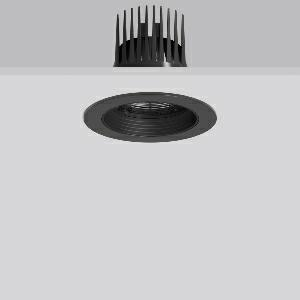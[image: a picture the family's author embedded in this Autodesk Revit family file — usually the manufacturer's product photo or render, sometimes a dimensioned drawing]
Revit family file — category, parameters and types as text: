
# Revit family: heledon_maxi_e_901767_003_1_76_1d41
name_source: partatom
category: Lighting Fixtures
units: mm (PartAtom-declared; Revit-internal decimal feet)

## family parameters
Cut with Voids When Loaded = No
Host = Face
Light Source = No
Part Type = Normal
Room Calculation Point = No
Round Connector Dimension = Use Diameter
Shared = No

## types (1)
- HELEDON maxi E (1 x LED Modul 940, 3900 lm, 4000)
    Apparent Load = 35 VA
    Approval mark = CE
    CIE Flux Codes = 97 100 100 100 100
    Color Rendering = 92
    Color Temperature = 4000
    Default Elevation = 1800 mm
    Description = Series: HELEDON maxi
Round recessed downlight. Housing: die-cast aluminium, powder-coated. Black plastic ring and recessed LED to prevent glare from the side. Optical assembly with lens made of plastic (polycarbonate) for the best homogeneous light distribution - can be changed without tools. Best colour rendering index Ra>90. Suitable for Recessed ceiling mounting. Installation without tools thanks to spring fastening system. Including separate LED converter with connecting cable 600 mm.High quality converter without flickering and stroboscopic effect. Through-wiring box (5 pole) available as accessory. The following accessories can be mounted without use of tools: interchangeable lenses, decorative glasses, honeycomb louvre, clear and frosted diffusers, white interchangeable plastic ring. 
Colour: deep black, matt (RAL 9005)
Diameter: 162 mm
Height: 3 mm
Cut-out diameter: 152 mm
Recess height: 200 mm
Luminaire: recess height: 135 mm
Lamp: LED
Socket: without socket
Colour temperature: 4000K
Colour rendering index (CRI): 92
System power: 35 W
Rated luminous flux: 3900 lm
Luminous efficiency: 111 lm/W
Control gear: Converter, dimmable, DALI
Protection class: II
Type of protection: IP 20
    Height = 0 mm  [stored 0 ft]
    Lamp = 1 x LED Modul 940
    Lamp Light Flux = 3900 lm
    Lamp count = 1
    Length = 162 mm
    Lifetime = 50000 h
    Luminous efficacy = 111 lm/W
    Manufacturer = RZB
    ModVariant = No
    Model = 901767.003.1.76
    Mounting Place = Ceiling
    Mounting Type = Recessed
    Number of Poles = 1
    OnlyDefault = Yes
    Power Factor = 1
    Product Name = HELEDON maxi E
    Product group = Recessed downlights
    ProductGroupID = 402
    Protection Class = Protection class II
    Protection Degree = IP 20
    RLX_Detail_Level = 1
    RLX_Emergency_Light_Flux = 0 lm
    RLX_Emergency_Type = 0
    RLX_Emergency_Type_DB = No
    RlxData = <blob elided: 122285 chars, md5=eb73b91a>
    Socket = socket
    Standby Power = 0 W
    System Light Flux = 3900 lm
    System Power = 35 W
    Type Comments = Product without accessories
    Type Image = 901663.003.jpg
    URL = http://relux.com
    VarID = ---
    Voltage = 230 V
    Voltage Range = 220-240 V
    Weight = 0.00 kg
    Width = 0 mm  [stored 0 ft]

note: [stored X ft] marks values corroborated as IEEE doubles in the binary element streams (Revit-internal decimal feet)

## geometry (parser evidence)
native form markers: Blend x4, Sweep x11
no freeform markers — native parametric forms only
